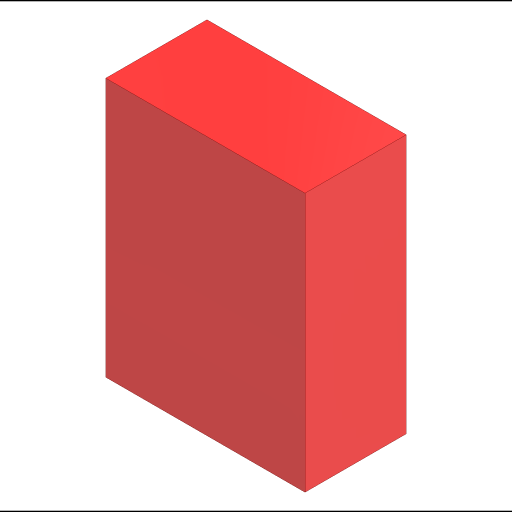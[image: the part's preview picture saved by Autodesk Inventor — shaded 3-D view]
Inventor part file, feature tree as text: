
AUTODESK INVENTOR PART (.ipt)
format: ipt  version: 2023 (Build 270158000, 158)  size: 89,088 bytes
history: native  units: in
note: dims shown in document units (in); Inventor stores cm internally (conversion verified against a paired STEP export)
features: extrude x1, sketch x1
ambient origin geometry x8: Origin, YZ Plane, XZ Plane, XY Plane, X Axis, Y Axis, Z Axis, Center Point
bodies: Solid1 (feature_tree)
feature tree (2):
  extrude  "Extrusion1"  Depth=0.5118in
  sketch  "Sketch1"  dims[d0=0.3937in d1=0.5118in d2=0.2in d3=0.0in]
